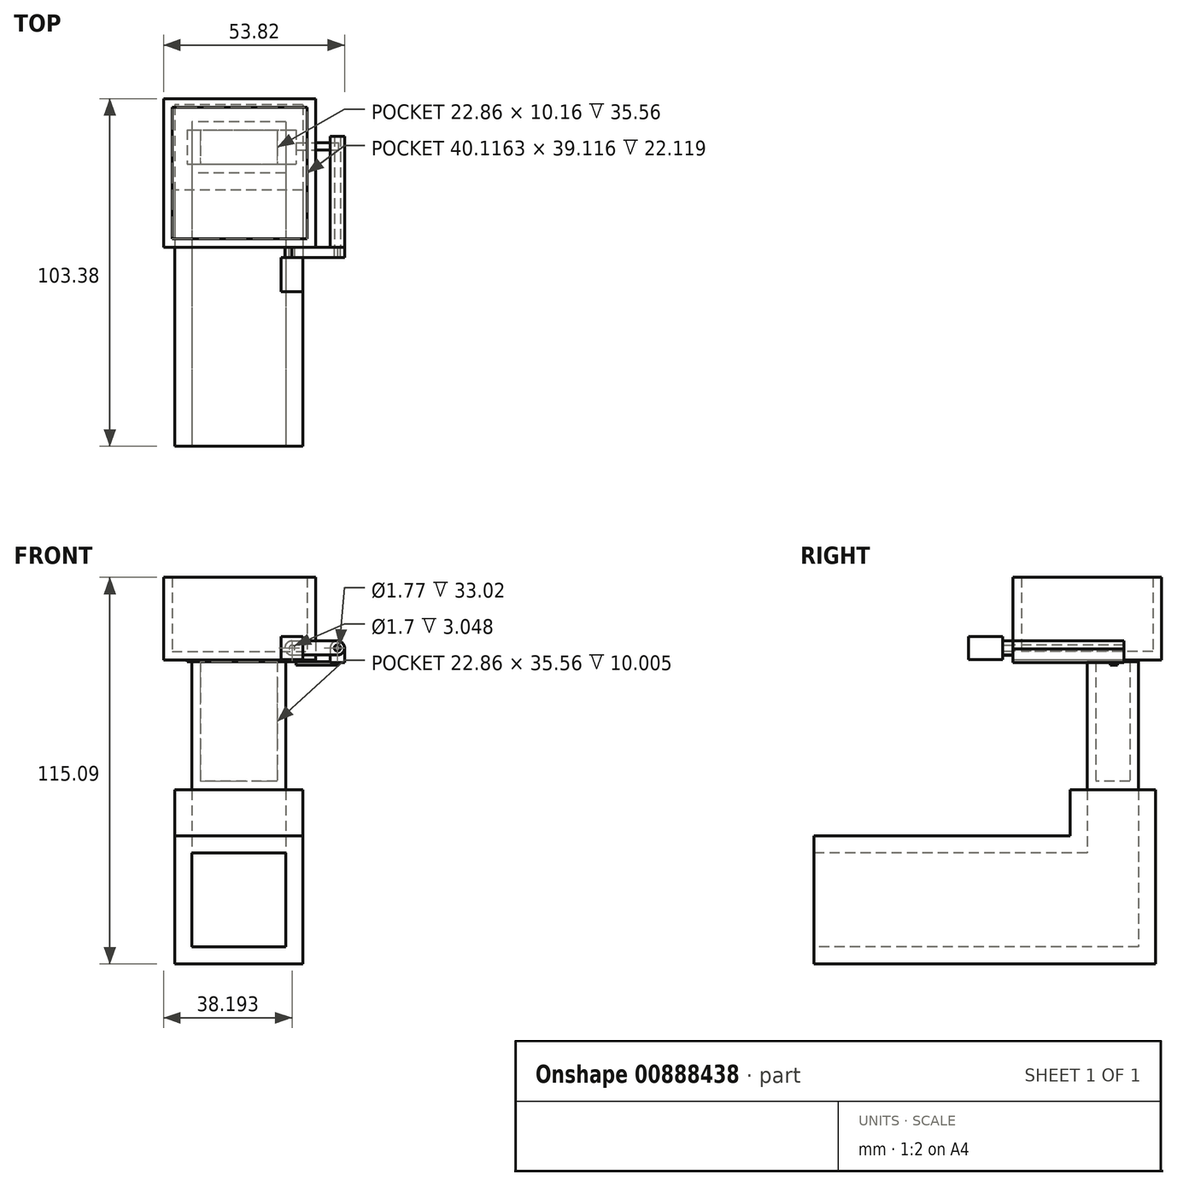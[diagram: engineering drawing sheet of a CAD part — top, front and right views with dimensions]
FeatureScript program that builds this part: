
annotation { "Feature Type Name" : "Feature", "Feature Type Description" : "" }
export const myFeature = defineFeature(function(context is Context, id is Id, definition is map)
    precondition{}
    {
        {
            var Q0;
            Q0=qCreatedBy(makeId("Front.planeOp"),FACE);
            var sketch = newSketch(context, id + "F0", { "sketchPlane" : qUnion([Q0])});
            skLineSegment(sketch, "E0.bottom", {"start": v(-15.86, 21.02) * mm, "end": v(22.24, 21.02) * mm});
            skLineSegment(sketch, "E0.top", {"start": v(-15.86, -17.08) * mm, "end": v(22.24, -17.08) * mm});
            skLineSegment(sketch, "E0.left", {"start": v(-15.86, 21.02) * mm, "end": v(-15.86, -17.08) * mm});
            skLineSegment(sketch, "E0.right", {"start": v(22.24, 21.02) * mm, "end": v(22.24, -17.08) * mm});
            skSolve(sketch);
        }
        {
            var Q0;
            Q0 = qSketchRegion(id + "F0", true);
            extrude(context, id + "F1", {"entities" : qUnion([Q0]), "oppositeDirection" : true, "depth" : 76.2 * mm, "offsetDistance" : 25.4 * mm});
        }
        {
            var Q0;
            Q0=makeQuery(id+"F1.opExtrude","CAP_FACE",FACE,{"disambiguationData":[OSD([sQuery(id+"F0.wireOp",EDGE,"E0.bottom"),sQuery(id+"F0.wireOp",EDGE,"E0.top"),sQuery(id+"F0.wireOp",EDGE,"E0.left"),sQuery(id+"F0.wireOp",EDGE,"E0.right")])],"isStart":false});
            var sketch = newSketch(context, id + "F2", { "sketchPlane" : qUnion([Q0])});
            skLineSegment(sketch, "E1.bottom", {"start": v(-22.24, -17.08) * mm, "end": v(15.86, -17.08) * mm});
            skLineSegment(sketch, "E1.top", {"start": v(-22.24, 34.74) * mm, "end": v(15.86, 34.74) * mm});
            skLineSegment(sketch, "E1.left", {"start": v(-22.24, -17.08) * mm, "end": v(-22.24, 34.74) * mm});
            skLineSegment(sketch, "E1.right", {"start": v(15.86, -17.08) * mm, "end": v(15.86, 34.74) * mm});
            skSolve(sketch);
        }
        {
            var Q0;
            Q0 = qSketchRegion(id + "F2", true);
            extrude(context, id + "F3", {"entities" : qUnion([Q0]), "operationType" : NewBodyOperationType.ADD, "depth" : 25.4 * mm, "offsetDistance" : 25.4 * mm});
        }
        {
            var Q0;
            Q0=makeQuery(id+"F3.opExtrude","SWEPT_FACE",FACE,{"disambiguationData":[OSD([sQuery(id+"F2.wireOp",EDGE,"E1.top")])]});
            shell(context, id + "F4", {"entities" : qUnion([Q0]), "thickness" : 5.08 * mm});
        }
        {
            var Q0;
            Q0=makeQuery(id+"F1.opExtrude","CAP_FACE",FACE,{"disambiguationData":[OSD([sQuery(id+"F0.wireOp",EDGE,"E0.bottom"),sQuery(id+"F0.wireOp",EDGE,"E0.top"),sQuery(id+"F0.wireOp",EDGE,"E0.left"),sQuery(id+"F0.wireOp",EDGE,"E0.right")])],"isStart":true});
            var sketch = newSketch(context, id + "F5", { "sketchPlane" : qUnion([Q0])});
            skLineSegment(sketch, "E2.bottom", {"start": v(-10.78, 15.94) * mm, "end": v(17.16, 15.94) * mm});
            skLineSegment(sketch, "E2.top", {"start": v(-10.78, -12) * mm, "end": v(17.16, -12) * mm});
            skLineSegment(sketch, "E2.left", {"start": v(-10.78, 15.94) * mm, "end": v(-10.78, -12) * mm});
            skLineSegment(sketch, "E2.right", {"start": v(17.16, 15.94) * mm, "end": v(17.16, -12) * mm});
            skSolve(sketch);
        }
        {
            var Q0;
            Q0 = qSketchRegion(id + "F5", true);
            extrude(context, id + "F6", {"entities" : qUnion([Q0]), "operationType" : NewBodyOperationType.REMOVE, "oppositeDirection" : true, "depth" : 25.4 * mm, "offsetDistance" : 25.4 * mm});
        }
        {
            var Q0;
            Q0=makeQuery(id+"F3.opExtrude","SWEPT_FACE",FACE,{"disambiguationData":[OSD([sQuery(id+"F2.wireOp",EDGE,"E1.top")])]});
            var sketch = newSketch(context, id + "F7", { "sketchPlane" : qUnion([Q0])});
            skLineSegment(sketch, "E3.bottom", {"start": v(-10.78, 81.28) * mm, "end": v(17.16, 81.28) * mm});
            skLineSegment(sketch, "E3.top", {"start": v(-10.78, 96.52) * mm, "end": v(17.16, 96.52) * mm});
            skLineSegment(sketch, "E3.left", {"start": v(-10.78, 81.28) * mm, "end": v(-10.78, 96.52) * mm});
            skLineSegment(sketch, "E3.right", {"start": v(17.16, 81.28) * mm, "end": v(17.16, 96.52) * mm});
            skSolve(sketch);
        }
        {
            var Q0;
            Q0=makeQuery(id+"F7.imprint","IMPRINT",FACE,{"disambiguationData":[TD([[makeQuery(id+"F7.imprint","IMPRINT",EDGE,{"derivedFrom":sQuery(id+"F7.wireOp",EDGE,"E3.bottom")}),-1.0]])]});
            extrude(context, id + "F8", {"entities" : qUnion([Q0]), "depth" : 38.1 * mm, "offsetDistance" : 25.4 * mm});
        }
        {
            var Q0;
            Q0=makeQuery(id+"F8.opExtrude","CAP_FACE",FACE,{"disambiguationData":[OSD([sQuery(id+"F7.wireOp",EDGE,"E3.bottom"),sQuery(id+"F7.wireOp",EDGE,"E3.top"),sQuery(id+"F7.wireOp",EDGE,"E3.left"),sQuery(id+"F7.wireOp",EDGE,"E3.right")])],"isStart":false});
            shell(context, id + "F9", {"entities" : qUnion([Q0]), "thickness" : 2.54 * mm});
        }
        {
            var Q0;
            Q0=makeQuery(id+"F8.opExtrude","CAP_FACE",FACE,{"disambiguationData":[OSD([sQuery(id+"F7.wireOp",EDGE,"E3.bottom"),sQuery(id+"F7.wireOp",EDGE,"E3.top"),sQuery(id+"F7.wireOp",EDGE,"E3.left"),sQuery(id+"F7.wireOp",EDGE,"E3.right")])],"isStart":false});
            var sketch = newSketch(context, id + "F10", { "sketchPlane" : qUnion([Q0])});
            skLineSegment(sketch, "E4.bottom", {"start": v(-12.1, 94.17) * mm, "end": v(20.2, 94.17) * mm});
            skLineSegment(sketch, "E4.top", {"start": v(-12.1, 83.98) * mm, "end": v(20.2, 83.98) * mm});
            skLineSegment(sketch, "E4.left", {"start": v(-12.1, 94.17) * mm, "end": v(-12.1, 83.98) * mm});
            skLineSegment(sketch, "E4.right", {"start": v(20.2, 94.17) * mm, "end": v(20.2, 83.98) * mm});
            skSolve(sketch);
        }
        {
            var Q0;
            Q0 = qSketchRegion(id + "F10", true);
            extrude(context, id + "F11", {"entities" : qUnion([Q0]), "operationType" : NewBodyOperationType.ADD, "depth" : 0.5 * mm, "offsetDistance" : 25.4 * mm});
        }
        {
            var Q0;
            Q0=makeQuery(id+"F8.opExtrude","SWEPT_FACE",FACE,{"disambiguationData":[OSD([sQuery(id+"F7.wireOp",EDGE,"E3.bottom")])]});
            var sketch = newSketch(context, id + "F12", { "sketchPlane" : qUnion([Q0])});
            skLineSegment(sketch, "E5.bottom", {"start": v(-19.13, 98.01) * mm, "end": v(26.06, 98.01) * mm});
            skLineSegment(sketch, "E5.top", {"start": v(-19.13, 73.35) * mm, "end": v(26.06, 73.35) * mm});
            skLineSegment(sketch, "E5.left", {"start": v(-19.13, 98.01) * mm, "end": v(-19.13, 73.35) * mm});
            skLineSegment(sketch, "E5.right", {"start": v(26.06, 98.01) * mm, "end": v(26.06, 73.35) * mm});
            skSolve(sketch);
        }
        {
            var Q0;
            Q0=makeQuery(id+"F12.imprint","IMPRINT",FACE,{"disambiguationData":[TD([[makeQuery(id+"F12.imprint","IMPRINT",EDGE,{"derivedFrom":sQuery(id+"F12.wireOp",EDGE,"E5.bottom")}),-1.0]])]});
            extrude(context, id + "F13", {"entities" : qUnion([Q0]), "endBound" : BoundingType.SYMMETRIC, "oppositeDirection" : true, "depth" : 44.2 * mm, "offsetDistance" : 25.4 * mm});
        }
        {
            var Q0;
            Q0=makeQuery(id+"F13.opExtrude","SWEPT_FACE",FACE,{"disambiguationData":[OSD([sQuery(id+"F12.wireOp",EDGE,"E5.bottom")])]});
            shell(context, id + "F14", {"entities" : qUnion([Q0]), "thickness" : 2.54 * mm});
        }
        {
            var Q0;
            Q0=makeQuery(id+"F13.opExtrude","CAP_FACE",FACE,{"disambiguationData":[OSD([sQuery(id+"F12.wireOp",EDGE,"E5.bottom"),sQuery(id+"F12.wireOp",EDGE,"E5.top"),sQuery(id+"F12.wireOp",EDGE,"E5.left"),sQuery(id+"F12.wireOp",EDGE,"E5.right")])],"isStart":true});
            var sketch = newSketch(context, id + "F15", { "sketchPlane" : qUnion([Q0])});
            skArc(sketch, "E6", {"start": v(19.13, 79.06) * mm, "mid": v(16.96, 76.9) * mm, "end": v(19.24, 74.86) * mm});
            skLineSegment(sketch, "E7", {"start": v(19.24, 74.86) * mm, "end": v(32.73, 74.86) * mm});
            skLineSegment(sketch, "E8", {"start": v(19, 79.06) * mm, "end": v(32.56, 79.06) * mm});
            skArc(sketch, "E9", {"start": v(32.4, 74.86) * mm, "mid": v(34.66, 76.88) * mm, "end": v(32.56, 79.06) * mm});
            skCircle(sketch, "E10", {"center": v(32.56, 76.96) * mm, "radius": 0.91 * mm});
            skCircle(sketch, "E11", {"center": v(19.06, 76.96) * mm, "radius": 0.85 * mm});
            skSolve(sketch);
        }
        {
            var Q0;
            Q0=makeQuery(id+"F15.imprint","IMPRINT",FACE,{"disambiguationData":[TD([[makeQuery(id+"F15.imprint","IMPRINT",EDGE,{"derivedFrom":sQuery(id+"F15.wireOp",EDGE,"E10")}),-1.0]])]});
            var Q1;
            Q1=makeQuery(id+"F15.imprint","IMPRINT",FACE,{"disambiguationData":[TD([[makeQuery(id+"F15.imprint","IMPRINT",EDGE,{"derivedFrom":sQuery(id+"F15.wireOp",EDGE,"E11")}),-1.0]])]});
            extrude(context, id + "F16", {"entities" : qUnion([Q0, Q1]), "operationType" : NewBodyOperationType.ADD, "depth" : 3.05 * mm, "offsetDistance" : 25.4 * mm});
        }
        {
            var Q0;
            Q0=makeQuery(id+"F16.opExtrude","CAP_FACE",FACE,{"disambiguationData":[OSD([sQuery(id+"F15.wireOp",EDGE,"E6"),sQuery(id+"F15.wireOp",EDGE,"E7"),sQuery(id+"F15.wireOp",EDGE,"E8"),sQuery(id+"F15.wireOp",EDGE,"E9"),sQuery(id+"F15.wireOp",EDGE,"E10"),sQuery(id+"F15.wireOp",EDGE,"E11")])],"isStart":true});
            var sketch = newSketch(context, id + "F17", { "sketchPlane" : qUnion([Q0])});
            skCircle(sketch, "E12", {"center": v(-32.56, 76.96) * mm, "radius": 2.13 * mm});
            skLineSegment(sketch, "E13", {"start": v(-30.43, 77.05) * mm, "end": v(-30.43, 72.68) * mm});
            skLineSegment(sketch, "E14", {"start": v(-34.66, 76.88) * mm, "end": v(-34.66, 72.68) * mm});
            skPoint(sketch, "E14.startSnap0", {"position": v(-34.66, 77.04) * mm});
            skLineSegment(sketch, "E15", {"start": v(-34.66, 72.68) * mm, "end": v(-30.43, 72.68) * mm});
            skSolve(sketch);
        }
        {
            var Q0;
            Q0 = qSketchRegion(id + "F17", true);
            extrude(context, id + "F18", {"entities" : qUnion([Q0]), "operationType" : NewBodyOperationType.ADD, "depth" : 33.02 * mm, "offsetDistance" : 25.4 * mm});
        }
        {
            var Q0;
            Q0=makeQuery(id+"F16.opExtrude","CAP_FACE",FACE,{"disambiguationData":[OSD([sQuery(id+"F15.wireOp",EDGE,"E6"),sQuery(id+"F15.wireOp",EDGE,"E7"),sQuery(id+"F15.wireOp",EDGE,"E8"),sQuery(id+"F15.wireOp",EDGE,"E9"),sQuery(id+"F15.wireOp",EDGE,"E10"),sQuery(id+"F15.wireOp",EDGE,"E11")])],"isStart":false});
            var sketch = newSketch(context, id + "F19", { "sketchPlane" : qUnion([Q0])});
            skCircle(sketch, "E16", {"center": v(32.56, 76.96) * mm, "radius": 0.89 * mm});
            skSolve(sketch);
        }
        {
            var Q0;
            Q0 = qSketchRegion(id + "F19", true);
            extrude(context, id + "F20", {"entities" : qUnion([Q0]), "operationType" : NewBodyOperationType.REMOVE, "endBound" : BoundingType.THROUGH_ALL, "oppositeDirection" : true, "depth" : 25.4 * mm, "offsetDistance" : 25.4 * mm});
        }
        {
            var Q0;
            Q0=makeQuery(id+"F16.opExtrude","CAP_FACE",FACE,{"disambiguationData":[OSD([sQuery(id+"F15.wireOp",EDGE,"E6"),sQuery(id+"F15.wireOp",EDGE,"E7"),sQuery(id+"F15.wireOp",EDGE,"E8"),sQuery(id+"F15.wireOp",EDGE,"E9"),sQuery(id+"F15.wireOp",EDGE,"E10"),sQuery(id+"F15.wireOp",EDGE,"E11")])],"isStart":false});
            var sketch = newSketch(context, id + "F21", { "sketchPlane" : qUnion([Q0])});
            skLineSegment(sketch, "E17.bottom", {"start": v(22.3, 80.37) * mm, "end": v(15.83, 80.37) * mm});
            skLineSegment(sketch, "E17.top", {"start": v(22.3, 73.55) * mm, "end": v(15.83, 73.55) * mm});
            skLineSegment(sketch, "E17.left", {"start": v(22.3, 80.37) * mm, "end": v(22.3, 73.55) * mm});
            skLineSegment(sketch, "E17.right", {"start": v(15.83, 80.37) * mm, "end": v(15.83, 73.55) * mm});
            skPoint(sketch, "E17.middle", {"position": v(19.06, 76.96) * mm});
            skSolve(sketch);
        }
        {
            var Q0;
            Q0 = qSketchRegion(id + "F21", true);
            extrude(context, id + "F22", {"entities" : qUnion([Q0]), "operationType" : NewBodyOperationType.ADD, "depth" : 10.16 * mm, "offsetDistance" : 25.4 * mm});
        }
        {
            var Q0;
            {var subQ0=sQuery(id+"F10.wireOp",EDGE,"E4.bottom");var subQ1=sQuery(id+"F7.wireOp",EDGE,"E3.right");var subQ2=sQuery(id+"F10.wireOp",EDGE,"E4.top");var subQ3=sQuery(id+"F10.wireOp",EDGE,"E4.right");Q0=makeQuery(id+"F11.boolean.opBoolean","SPLIT",FACE,{"disambiguationData":[TD([makeQuery(id+"F8.opExtrude","SWEPT_FACE",FACE,{"disambiguationData":[OSD([subQ1])]})])],"derivedFrom":makeQuery(id+"F11.opExtrude","CAP_FACE",FACE,{"disambiguationData":[OSD([subQ0,subQ2,sQuery(id+"F10.wireOp",EDGE,"E4.left"),subQ3])],"isStart":true})});}
            var sketch = newSketch(context, id + "F23", { "sketchPlane" : qUnion([Q0])});
            skLineSegment(sketch, "E18.bottom", {"start": v(18.73, -88.15) * mm, "end": v(33, -88.15) * mm});
            skLineSegment(sketch, "E18.top", {"start": v(18.73, -90.32) * mm, "end": v(33, -90.32) * mm});
            skLineSegment(sketch, "E18.left", {"start": v(18.73, -88.15) * mm, "end": v(18.73, -90.32) * mm});
            skLineSegment(sketch, "E18.right", {"start": v(33, -88.15) * mm, "end": v(33, -90.32) * mm});
            skSolve(sketch);
        }
        {
            var Q0;
            {var subQ0=sQuery(id+"F23.wireOp",EDGE,"E18.right");Q0=makeQuery(id+"F23.imprint","IMPRINT",FACE,{"disambiguationData":[TD([[makeQuery(id+"F23.imprint","IMPRINT",EDGE,{"derivedFrom":subQ0}),-1.0]])]});}
            extrude(context, id + "F24", {"entities" : qUnion([Q0]), "depth" : 1.02 * mm, "offsetDistance" : 25.4 * mm});
        }
    });
